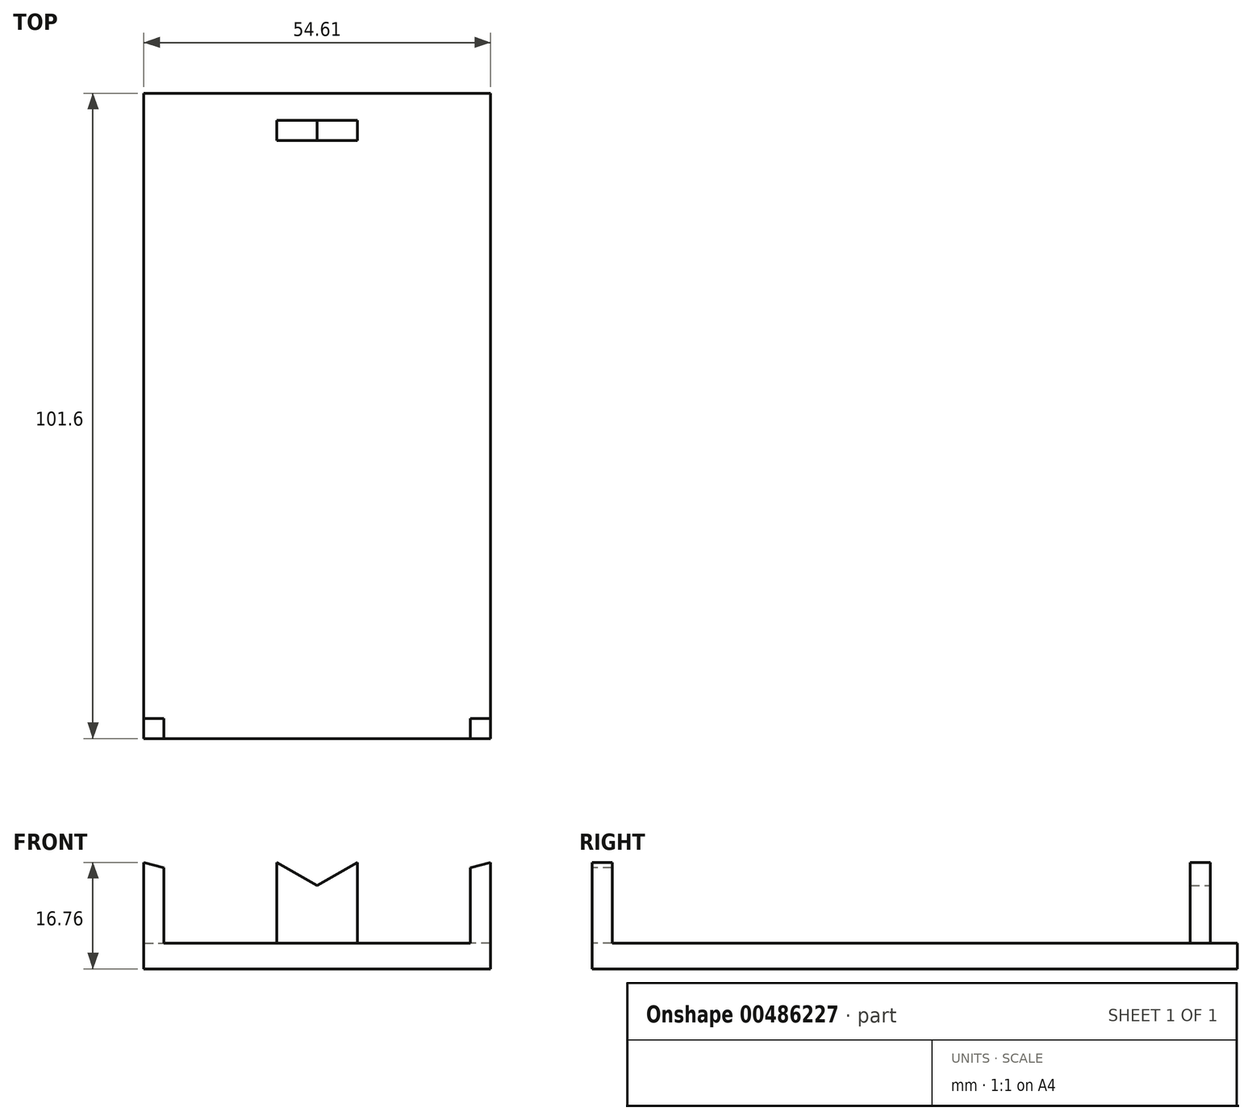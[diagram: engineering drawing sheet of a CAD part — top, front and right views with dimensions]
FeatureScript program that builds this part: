
annotation { "Feature Type Name" : "Feature", "Feature Type Description" : "" }
export const myFeature = defineFeature(function(context is Context, id is Id, definition is map)
    precondition{}
    {
        {
            var Q0;
            Q0=qCreatedBy(makeId("Top.planeOp"),FACE);
            var sketch = newSketch(context, id + "F0", { "sketchPlane" : qUnion([Q0])});
            skLineSegment(sketch, "E0.bottom", {"start": v(27.3, -50.8) * mm, "end": v(-27.3, -50.8) * mm});
            skLineSegment(sketch, "E0.top", {"start": v(27.3, 50.8) * mm, "end": v(-27.3, 50.8) * mm});
            skLineSegment(sketch, "E0.left", {"start": v(27.3, -50.8) * mm, "end": v(27.3, 50.8) * mm});
            skLineSegment(sketch, "E0.right", {"start": v(-27.3, -50.8) * mm, "end": v(-27.3, 50.8) * mm});
            skPoint(sketch, "E0.middle", {"position": v(0, 0) * mm});
            skSolve(sketch);
        }
        {
            var Q0;
            Q0 = qSketchRegion(id + "F0", true);
            extrude(context, id + "F1", {"entities" : qUnion([Q0]), "depth" : 4.06 * mm, "offsetDistance" : 25.4 * mm});
        }
        {
            var Q0;
            Q0=makeQuery(id+"F1.opExtrude","CAP_FACE",FACE,{"disambiguationData":[OSD([sQuery(id+"F0.wireOp",EDGE,"E0.bottom"),sQuery(id+"F0.wireOp",EDGE,"E0.top"),sQuery(id+"F0.wireOp",EDGE,"E0.left"),sQuery(id+"F0.wireOp",EDGE,"E0.right")])],"isStart":false});
            var sketch = newSketch(context, id + "F2", { "sketchPlane" : qUnion([Q0])});
            skLineSegment(sketch, "E1.bottom", {"start": v(6.35, 43.34) * mm, "end": v(-6.35, 43.34) * mm});
            skLineSegment(sketch, "E1.top", {"start": v(6.35, 46.52) * mm, "end": v(-6.35, 46.52) * mm});
            skLineSegment(sketch, "E1.left", {"start": v(6.35, 43.34) * mm, "end": v(6.35, 46.52) * mm});
            skLineSegment(sketch, "E1.right", {"start": v(-6.35, 43.34) * mm, "end": v(-6.35, 46.52) * mm});
            skPoint(sketch, "E1.middle", {"position": v(0, 44.93) * mm});
            skSolve(sketch);
        }
        {
            var Q0;
            Q0 = qSketchRegion(id + "F2", true);
            extrude(context, id + "F3", {"entities" : qUnion([Q0]), "operationType" : NewBodyOperationType.ADD, "depth" : 12.7 * mm, "offsetDistance" : 25.4 * mm});
        }
        {
            var Q0;
            Q0=makeQuery(id+"F3.opExtrude","SWEPT_FACE",FACE,{"disambiguationData":[OSD([sQuery(id+"F2.wireOp",EDGE,"E1.top")])]});
            var sketch = newSketch(context, id + "F4", { "sketchPlane" : qUnion([Q0])});
            skLineSegment(sketch, "E2", {"start": v(0, 16.76) * mm, "end": v(0, 13.1) * mm, "construction": true});
            skLineSegment(sketch, "E3", {"start": v(0, 13.1) * mm, "end": v(-6.35, 16.76) * mm});
            skLineSegment(sketch, "E4", {"start": v(-6.35, 16.76) * mm, "end": v(0, 13.1) * mm});
            skLineSegment(sketch, "E5", {"start": v(6.35, 16.76) * mm, "end": v(0, 13.1) * mm});
            skLineSegment(sketch, "E6", {"start": v(-6.35, 16.76) * mm, "end": v(6.35, 16.76) * mm});
            skSolve(sketch);
        }
        {
            var Q0;
            Q0 = qSketchRegion(id + "F4", true);
            extrude(context, id + "F5", {"entities" : qUnion([Q0]), "operationType" : NewBodyOperationType.REMOVE, "oppositeDirection" : true, "depth" : 25.4 * mm, "offsetDistance" : 25.4 * mm});
        }
        {
            var Q0;
            Q0=makeQuery(id+"F1.opExtrude","CAP_FACE",FACE,{"disambiguationData":[OSD([sQuery(id+"F0.wireOp",EDGE,"E0.bottom"),sQuery(id+"F0.wireOp",EDGE,"E0.top"),sQuery(id+"F0.wireOp",EDGE,"E0.left"),sQuery(id+"F0.wireOp",EDGE,"E0.right")])],"isStart":false});
            var sketch = newSketch(context, id + "F6", { "sketchPlane" : qUnion([Q0])});
            skLineSegment(sketch, "E7.bottom", {"start": v(-27.3, -47.62) * mm, "end": v(-24.13, -47.62) * mm});
            skLineSegment(sketch, "E7.top", {"start": v(-27.3, -50.8) * mm, "end": v(-24.13, -50.8) * mm});
            skLineSegment(sketch, "E7.left", {"start": v(-27.3, -47.62) * mm, "end": v(-27.3, -50.8) * mm});
            skLineSegment(sketch, "E7.right", {"start": v(-24.13, -47.62) * mm, "end": v(-24.13, -50.8) * mm});
            skPoint(sketch, "E8.oppositeSnap0", {"position": v(0, -50.8) * mm});
            skLineSegment(sketch, "E8.bottom", {"start": v(0, -50.8) * mm, "end": v(0, -50.8) * mm});
            skLineSegment(sketch, "E8.top", {"start": v(0, -36.58) * mm, "end": v(0, -36.58) * mm});
            skLineSegment(sketch, "E8.left", {"start": v(0, -50.8) * mm, "end": v(0, -36.58) * mm, "construction": true});
            skLineSegment(sketch, "E8.right", {"start": v(0, -50.8) * mm, "end": v(0, -36.58) * mm, "construction": true});
            skLineSegment(sketch, "E9.MirrorCS", {"start": v(24.13, -47.62) * mm, "end": v(24.13, -50.8) * mm});
            skLineSegment(sketch, "E10.MirrorCS", {"start": v(27.3, -47.62) * mm, "end": v(24.13, -47.62) * mm});
            skLineSegment(sketch, "E11.MirrorCS", {"start": v(27.3, -47.62) * mm, "end": v(27.3, -50.8) * mm});
            skLineSegment(sketch, "E12.MirrorCS", {"start": v(27.3, -50.8) * mm, "end": v(24.13, -50.8) * mm});
            skSolve(sketch);
        }
        {
            var Q0;
            Q0 = qSketchRegion(id + "F6", true);
            extrude(context, id + "F7", {"entities" : qUnion([Q0]), "operationType" : NewBodyOperationType.ADD, "depth" : 12.7 * mm, "offsetDistance" : 25.4 * mm});
        }
        {
            var Q0;
            Q0=makeQuery(id+"F7.boolean.opBoolean","MERGE",FACE,{"derivedFrom":[makeQuery(id+"F1.opExtrude","SWEPT_FACE",FACE,{"disambiguationData":[OSD([sQuery(id+"F0.wireOp",EDGE,"E0.bottom")])]}),makeQuery(id+"F7.opExtrude","SWEPT_FACE",FACE,{"disambiguationData":[OSD([sQuery(id+"F6.wireOp",EDGE,"E7.top")])]}),makeQuery(id+"F7.opExtrude","SWEPT_FACE",FACE,{"disambiguationData":[OSD([sQuery(id+"F6.wireOp",EDGE,"E12.MirrorCS")])]})]});
            var sketch = newSketch(context, id + "F8", { "sketchPlane" : qUnion([Q0])});
            skLineSegment(sketch, "E13", {"start": v(27.3, 16.76) * mm, "end": v(24.13, 15.91) * mm});
            skLineSegment(sketch, "E14", {"start": v(24.13, 15.91) * mm, "end": v(24.13, 16.76) * mm});
            skLineSegment(sketch, "E15", {"start": v(24.13, 16.76) * mm, "end": v(27.3, 16.76) * mm});
            skLineSegment(sketch, "E16", {"start": v(-24.13, 16.76) * mm, "end": v(-24.13, 15.9) * mm});
            skLineSegment(sketch, "E17", {"start": v(-27.3, 16.76) * mm, "end": v(-24.13, 15.9) * mm});
            skLineSegment(sketch, "E18", {"start": v(-24.13, 16.76) * mm, "end": v(-27.3, 16.76) * mm});
            skSolve(sketch);
        }
        {
            var Q0;
            Q0=makeQuery(id+"F8.imprint","IMPRINT",FACE,{"disambiguationData":[TD([[makeQuery(id+"F8.imprint","IMPRINT",EDGE,{"derivedFrom":sQuery(id+"F8.wireOp",EDGE,"E16")}),-1.0]])]});
            var Q1;
            Q1=makeQuery(id+"F8.imprint","IMPRINT",FACE,{"disambiguationData":[TD([[makeQuery(id+"F8.imprint","IMPRINT",EDGE,{"derivedFrom":sQuery(id+"F8.wireOp",EDGE,"E13")}),-1.0]])]});
            extrude(context, id + "F9", {"entities" : qUnion([Q0, Q1]), "operationType" : NewBodyOperationType.REMOVE, "oppositeDirection" : true, "depth" : 25.4 * mm, "offsetDistance" : 25.4 * mm});
        }
    });
